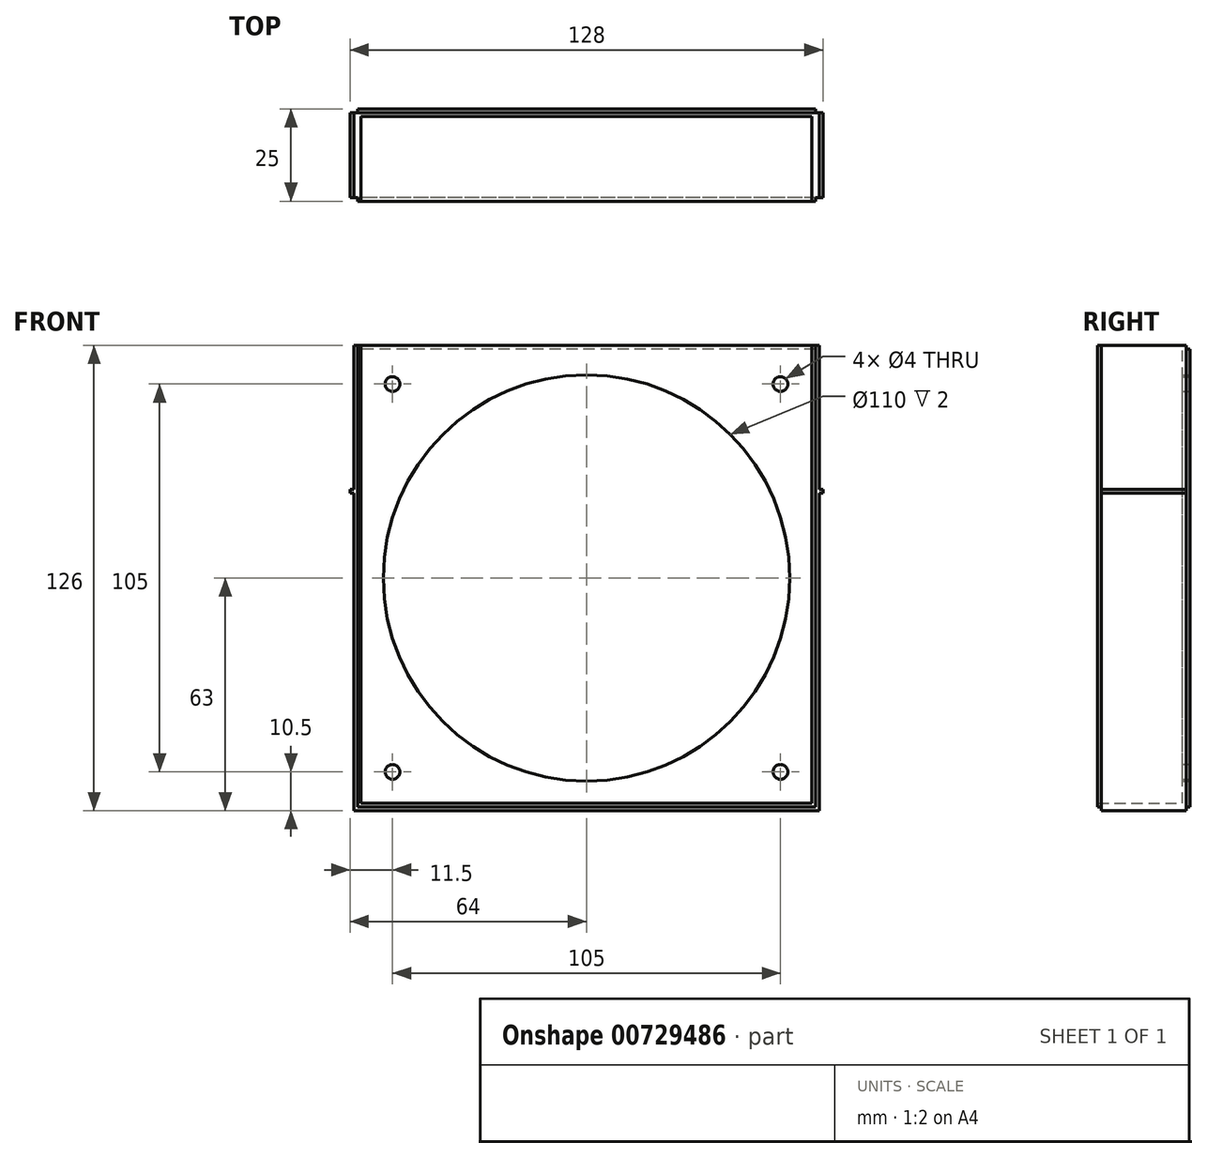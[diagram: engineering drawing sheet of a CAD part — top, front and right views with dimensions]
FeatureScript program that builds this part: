
annotation { "Feature Type Name" : "Feature", "Feature Type Description" : "" }
export const myFeature = defineFeature(function(context is Context, id is Id, definition is map)
    precondition{}
    {
        {
            var Q0;
            Q0=qCreatedBy(makeId("Front.planeOp"),FACE);
            var sketch = newSketch(context, id + "F0", { "sketchPlane" : qUnion([Q0])});
            skLineSegment(sketch, "E0.bottom", {"start": v(61, -61) * mm, "end": v(-61, -61) * mm});
            skLineSegment(sketch, "E0.top", {"start": v(61, 61) * mm, "end": v(-61, 61) * mm});
            skLineSegment(sketch, "E0.left", {"start": v(61, -61) * mm, "end": v(61, 61) * mm});
            skLineSegment(sketch, "E0.right", {"start": v(-61, -61) * mm, "end": v(-61, 61) * mm});
            skPoint(sketch, "E0.middle", {"position": v(0, 0) * mm});
            skLineSegment(sketch, "E1.0", {"start": v(62, 62) * mm, "end": v(-62, 62) * mm});
            skLineSegment(sketch, "E1.1", {"start": v(62, -62) * mm, "end": v(62, 62) * mm});
            skLineSegment(sketch, "E1.2", {"start": v(62, -62) * mm, "end": v(-62, -62) * mm});
            skLineSegment(sketch, "E1.3", {"start": v(-62, -62) * mm, "end": v(-62, 62) * mm});
            skLineSegment(sketch, "E2.0", {"start": v(-63, -63) * mm, "end": v(-63, 63) * mm});
            skLineSegment(sketch, "E2.1", {"start": v(63, -63) * mm, "end": v(-63, -63) * mm});
            skLineSegment(sketch, "E2.2", {"start": v(63, -63) * mm, "end": v(63, 63) * mm});
            skLineSegment(sketch, "E2.3", {"start": v(63, 63) * mm, "end": v(-63, 63) * mm});
            skCircle(sketch, "E3", {"center": v(0, 0) * mm, "radius": 55 * mm});
            skPoint(sketch, "E4", {"position": v(-52.5, 52.5) * mm});
            skPoint(sketch, "E5", {"position": v(52.5, 52.5) * mm});
            skPoint(sketch, "E6", {"position": v(52.5, -52.5) * mm});
            skPoint(sketch, "E7", {"position": v(-52.5, -52.5) * mm});
            skCircle(sketch, "E8", {"center": v(-52.5, 52.5) * mm, "radius": 2 * mm});
            skCircle(sketch, "E9", {"center": v(52.5, 52.5) * mm, "radius": 2 * mm});
            skCircle(sketch, "E10", {"center": v(52.5, -52.5) * mm, "radius": 2 * mm});
            skCircle(sketch, "E11", {"center": v(-52.5, -52.5) * mm, "radius": 2 * mm});
            skLineSegment(sketch, "E12", {"start": v(-61, 61) * mm, "end": v(-61, 62) * mm});
            skLineSegment(sketch, "E13", {"start": v(-61, 62) * mm, "end": v(-61, 63) * mm});
            skLineSegment(sketch, "E14", {"start": v(61, 61) * mm, "end": v(61, 62) * mm});
            skLineSegment(sketch, "E15", {"start": v(61, 62) * mm, "end": v(61, 63) * mm});
            skLineSegment(sketch, "E16", {"start": v(-62, 62) * mm, "end": v(-62, 63) * mm});
            skLineSegment(sketch, "E17", {"start": v(62, 62) * mm, "end": v(62, 63) * mm});
            skSolve(sketch);
        }
        {
            var Q0;
            Q0=makeQuery(id+"F0.imprint","IMPRINT",FACE,{"disambiguationData":[TD([[makeQuery(id+"F0.imprint","IMPRINT",EDGE,{"derivedFrom":sQuery(id+"F0.wireOp",EDGE,"E0.bottom")}),-1.0]])]});
            var Q1;
            Q1=makeQuery(id+"F0.imprint","IMPRINT",FACE,{"disambiguationData":[TD([[makeQuery(id+"F0.imprint","IMPRINT",EDGE,{"derivedFrom":sQuery(id+"F0.wireOp",EDGE,"E0.top")}),-1.0]])]});
            var Q2;
            {var subQ0=sQuery(id+"F0.wireOp",EDGE,"E13");Q2=makeQuery(id+"F0.imprint","IMPRINT",FACE,{"disambiguationData":[TD([[makeQuery(id+"F0.imprint","IMPRINT",EDGE,{"derivedFrom":subQ0}),-1.0]])]});}
            extrude(context, id + "F1", {"entities" : qUnion([Q0, Q1, Q2]), "depth" : 2 * mm, "offsetDistance" : 25 * mm});
        }
        {
            var Q0;
            Q0=makeQuery(id+"F0.imprint","IMPRINT",FACE,{"disambiguationData":[TD([[makeQuery(id+"F0.imprint","IMPRINT",EDGE,{"derivedFrom":sQuery(id+"F0.wireOp",EDGE,"E0.bottom")}),1.0]])]});
            var Q1;
            {var subQ2=sQuery(id+"F0.wireOp",EDGE,"E15");Q1=makeQuery(id+"F0.imprint","IMPRINT",FACE,{"disambiguationData":[TD([[makeQuery(id+"F0.imprint","IMPRINT",EDGE,{"derivedFrom":subQ2}),-1.0]])]});}
            var Q2;
            {var subQ2=sQuery(id+"F0.wireOp",EDGE,"E13");Q2=makeQuery(id+"F0.imprint","IMPRINT",FACE,{"disambiguationData":[TD([[makeQuery(id+"F0.imprint","IMPRINT",EDGE,{"derivedFrom":subQ2}),1.0]])]});}
            extrude(context, id + "F2", {"entities" : qUnion([Q0, Q1, Q2]), "operationType" : NewBodyOperationType.ADD, "depth" : 25 * mm, "offsetDistance" : 25 * mm});
        }
        {
            var Q0;
            Q0=makeQuery(id+"F0.imprint","IMPRINT",FACE,{"disambiguationData":[TD([[makeQuery(id+"F0.imprint","IMPRINT",EDGE,{"derivedFrom":sQuery(id+"F0.wireOp",EDGE,"E1.1")}),-1.0]])]});
            extrude(context, id + "F3", {"entities" : qUnion([Q0]), "operationType" : NewBodyOperationType.ADD, "depth" : 24 * mm, "offsetDistance" : 25 * mm});
        }
        {
            var Q0;
            Q0=makeQuery(id+"F0.imprint","IMPRINT",FACE,{"disambiguationData":[TD([[makeQuery(id+"F0.imprint","IMPRINT",EDGE,{"derivedFrom":sQuery(id+"F0.wireOp",EDGE,"E1.1")}),-1.0]])]});
            var Q1;
            {var subQ2=sQuery(id+"F0.wireOp",EDGE,"E15");Q1=makeQuery(id+"F0.imprint","IMPRINT",FACE,{"disambiguationData":[TD([[makeQuery(id+"F0.imprint","IMPRINT",EDGE,{"derivedFrom":subQ2}),-1.0]])]});}
            var Q2;
            {var subQ0=sQuery(id+"F0.wireOp",EDGE,"E13");Q2=makeQuery(id+"F0.imprint","IMPRINT",FACE,{"disambiguationData":[TD([[makeQuery(id+"F0.imprint","IMPRINT",EDGE,{"derivedFrom":subQ0}),-1.0]])]});}
            var Q3;
            {var subQ2=sQuery(id+"F0.wireOp",EDGE,"E13");Q3=makeQuery(id+"F0.imprint","IMPRINT",FACE,{"disambiguationData":[TD([[makeQuery(id+"F0.imprint","IMPRINT",EDGE,{"derivedFrom":subQ2}),1.0]])]});}
            extrude(context, id + "F4", {"entities" : qUnion([Q0, Q1, Q2, Q3]), "operationType" : NewBodyOperationType.REMOVE, "depth" : 1 * mm, "offsetDistance" : 25 * mm});
        }
        {
            var Q0;
            Q0=makeQuery(id+"F3.opExtrude","SWEPT_FACE",FACE,{"disambiguationData":[OSD([sQuery(id+"F0.wireOp",EDGE,"E2.0")])]});
            var sketch = newSketch(context, id + "F5", { "sketchPlane" : qUnion([Q0])});
            skLineSegment(sketch, "E18", {"start": v(1, 23) * mm, "end": v(24, 23) * mm});
            skLineSegment(sketch, "E19.0", {"start": v(1, 24) * mm, "end": v(24, 24) * mm});
            skSolve(sketch);
        }
        {
            var Q0;
            {var subQ0=sQuery(id+"F5.wireOp",EDGE,"E18");Q0=makeQuery(id+"F5.imprint","IMPRINT",FACE,{"disambiguationData":[TD([[makeQuery(id+"F5.imprint","IMPRINT",EDGE,{"derivedFrom":subQ0}),1.0]])]});}
            extrude(context, id + "F6", {"entities" : qUnion([Q0]), "operationType" : NewBodyOperationType.ADD, "depth" : 1 * mm, "offsetDistance" : 25 * mm});
        }
        {
            var Q0;
            Q0=makeQuery(id+"F3.opExtrude","SWEPT_FACE",FACE,{"disambiguationData":[OSD([sQuery(id+"F0.wireOp",EDGE,"E2.2")])]});
            var sketch = newSketch(context, id + "F7", { "sketchPlane" : qUnion([Q0])});
            skLineSegment(sketch, "E20", {"start": v(-24, 23) * mm, "end": v(-1, 23) * mm});
            skLineSegment(sketch, "E21.0", {"start": v(-24, 24) * mm, "end": v(-1, 24) * mm});
            skSolve(sketch);
        }
        {
            var Q0;
            {var subQ0=sQuery(id+"F7.wireOp",EDGE,"E20");Q0=makeQuery(id+"F7.imprint","IMPRINT",FACE,{"disambiguationData":[TD([[makeQuery(id+"F7.imprint","IMPRINT",EDGE,{"derivedFrom":subQ0}),1.0]])]});}
            extrude(context, id + "F8", {"entities" : qUnion([Q0]), "operationType" : NewBodyOperationType.ADD, "depth" : 1 * mm, "offsetDistance" : 25 * mm});
        }
    });
